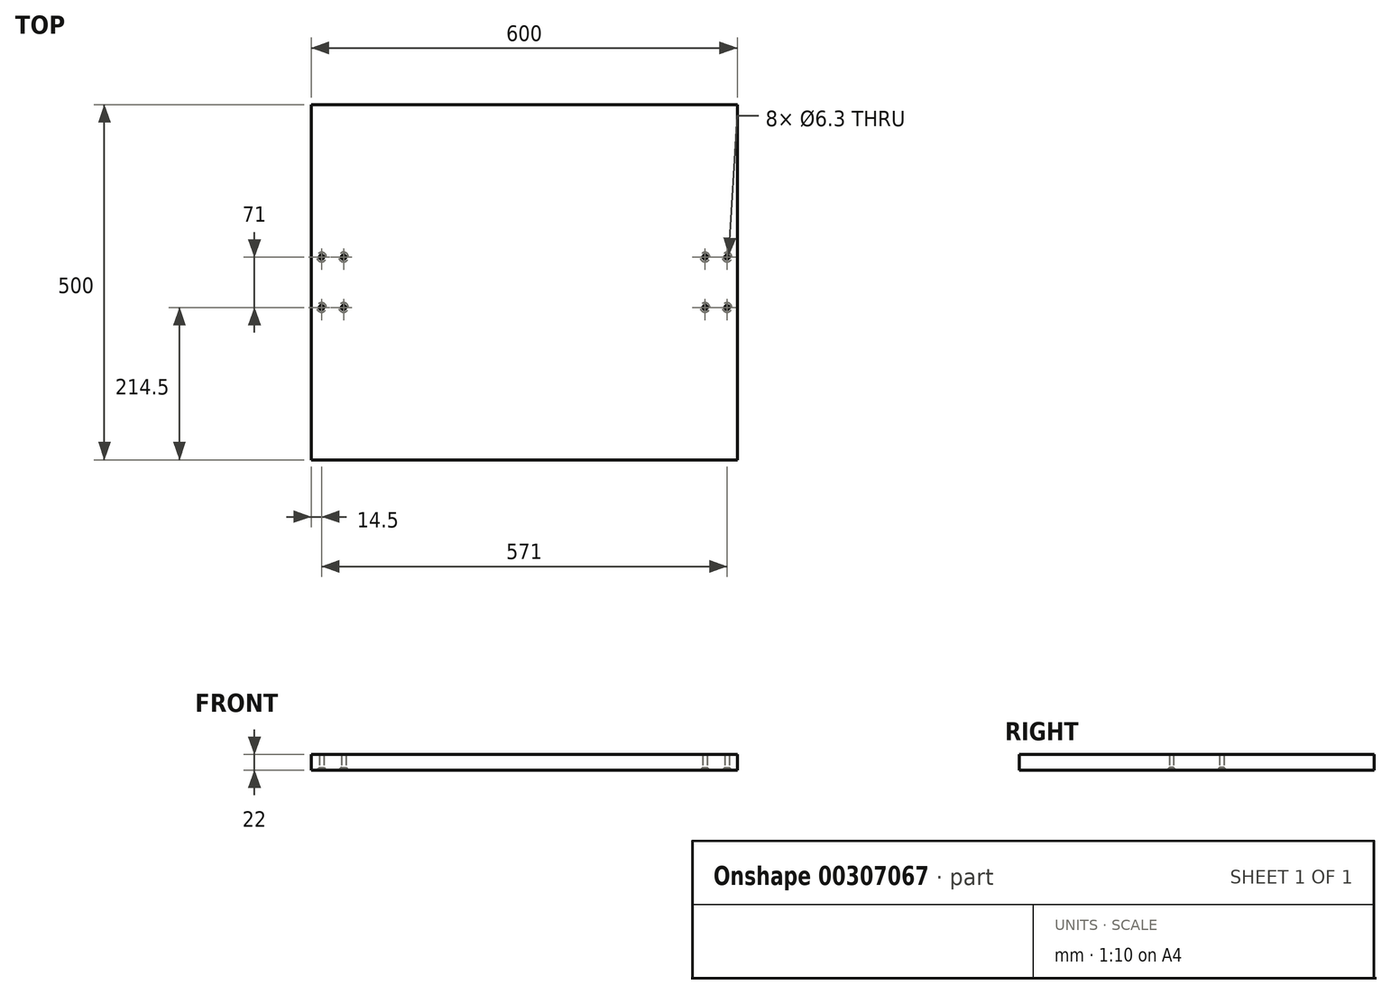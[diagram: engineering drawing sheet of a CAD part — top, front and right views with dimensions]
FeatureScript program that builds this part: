
annotation { "Feature Type Name" : "Feature", "Feature Type Description" : "" }
export const myFeature = defineFeature(function(context is Context, id is Id, definition is map)
    precondition{}
    {
        {
            var Q0;
            Q0=qCreatedBy(makeId("Top.planeOp"),FACE);
            var sketch = newSketch(context, id + "F0", { "sketchPlane" : qUnion([Q0])});
            skLineSegment(sketch, "E0.bottom", {"start": v(0, 0) * mm, "end": v(600, 0) * mm});
            skLineSegment(sketch, "E0.top", {"start": v(0, 500) * mm, "end": v(600, 500) * mm});
            skLineSegment(sketch, "E0.left", {"start": v(0, 0) * mm, "end": v(0, 500) * mm});
            skLineSegment(sketch, "E0.right", {"start": v(600, 0) * mm, "end": v(600, 500) * mm});
            skSolve(sketch);
        }
        {
            var Q0;
            Q0=makeQuery(id+"F0.imprint","IMPRINT",FACE,{"disambiguationData":[TD([[makeQuery(id+"F0.imprint","IMPRINT",EDGE,{"derivedFrom":sQuery(id+"F0.wireOp",EDGE,"E0.bottom")}),1.0]])]});
            extrude(context, id + "F1", {"entities" : qUnion([Q0]), "depth" : 22 * mm});
        }
        {
            var Q0;
            Q0=makeQuery(id+"F1.opExtrude","CAP_FACE",FACE,{"disambiguationData":[OSD([sQuery(id+"F0.wireOp",EDGE,"E0.bottom"),sQuery(id+"F0.wireOp",EDGE,"E0.top"),sQuery(id+"F0.wireOp",EDGE,"E0.left"),sQuery(id+"F0.wireOp",EDGE,"E0.right")])],"isStart":true});
            var sketch = newSketch(context, id + "F2", { "sketchPlane" : qUnion([Q0])});
            skPoint(sketch, "E1", {"position": v(14.5, -285.5) * mm});
            skPoint(sketch, "E2", {"position": v(554.5, -285.5) * mm});
            skPoint(sketch, "E3.0.1.0", {"position": v(14.5, -214.5) * mm});
            skPoint(sketch, "E3.0.1.1", {"position": v(554.5, -214.5) * mm});
            skPoint(sketch, "E3.1.0.0", {"position": v(45.5, -285.5) * mm});
            skPoint(sketch, "E3.1.0.1", {"position": v(585.5, -285.5) * mm});
            skPoint(sketch, "E3.1.1.0", {"position": v(45.5, -214.5) * mm});
            skPoint(sketch, "E3.1.1.1", {"position": v(585.5, -214.5) * mm});
            skLineSegment(sketch, "E3.direction1", {"start": v(14.5, -285.5) * mm, "end": v(45.5, -285.5) * mm, "construction": true});
            skLineSegment(sketch, "E3.direction2", {"start": v(14.5, -285.5) * mm, "end": v(14.5, -214.5) * mm, "construction": true});
            skSolve(sketch);
        }
        {
            var Q0;
            Q0=sQuery(id+"F2.wireOp",VERTEX,"E3.0.1.0");
            var Q1;
            Q1=sQuery(id+"F2.wireOp",VERTEX,"E3.1.1.0");
            var Q2;
            Q2=sQuery(id+"F2.wireOp",VERTEX,"E1");
            var Q3;
            Q3=sQuery(id+"F2.wireOp",VERTEX,"E3.1.0.0");
            var Q4;
            Q4=sQuery(id+"F2.wireOp",VERTEX,"E3.0.1.1");
            var Q5;
            Q5=sQuery(id+"F2.wireOp",VERTEX,"E3.1.1.1");
            var Q6;
            Q6=sQuery(id+"F2.wireOp",VERTEX,"E2");
            var Q7;
            Q7=sQuery(id+"F2.wireOp",VERTEX,"E3.1.0.1");
            var Q8;
            Q8=makeQuery(id+"F1.opExtrude","SWEPT_BODY",BODY,{"disambiguationData":[OSD([sQuery(id+"F0.wireOp",EDGE,"E0.bottom"),sQuery(id+"F0.wireOp",EDGE,"E0.top"),sQuery(id+"F0.wireOp",EDGE,"E0.left"),sQuery(id+"F0.wireOp",EDGE,"E0.right")])]});
            hole(context, id + "F3", {"style" : HoleStyle.C_SINK, "endStyle" : HoleEndStyle.THROUGH, "standardTappedOrClearance" : lookupTablePath({ "standard" : "ISO", "fit" : "Close", "size" : "M6", "type" : "Clearance" }), "standardBlindInLast" : lookupTablePath({ "fit" : "Close", "standard" : "ISO", "size" : "M6", "type" : "Clearance" }), "holeDiameter" : 6.3 * mm, "cSinkDiameter" : 13.44 * mm, "cSinkAngle" : 90 * degree, "tappedDepth" : 12 * mm, "tapClearance" : 3, "locations" : qUnion([Q0, Q1, Q2, Q3, Q4, Q5, Q6, Q7]), "scope" : qUnion([Q8])});
        }
    });
